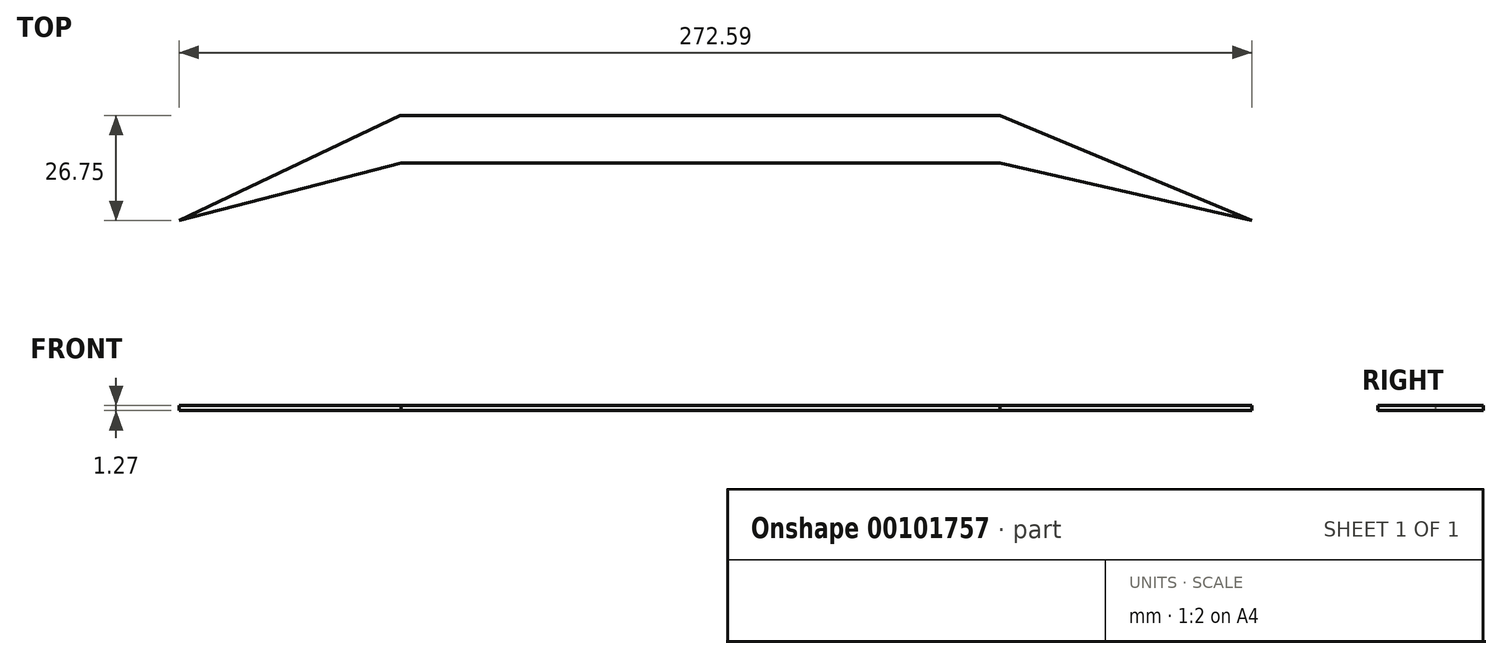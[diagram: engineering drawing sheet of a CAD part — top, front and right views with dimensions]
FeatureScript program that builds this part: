
annotation { "Feature Type Name" : "Feature", "Feature Type Description" : "" }
export const myFeature = defineFeature(function(context is Context, id is Id, definition is map)
    precondition{}
    {
        {
            var Q0;
            Q0=qCreatedBy(makeId("Top.planeOp"),FACE);
            var sketch = newSketch(context, id + "F0", { "sketchPlane" : qUnion([Q0])});
            skLineSegment(sketch, "E0", {"start": v(-136.18, 0) * mm, "end": v(-80.07, 26.75) * mm});
            skLineSegment(sketch, "E1", {"start": v(-80.07, 26.75) * mm, "end": v(0, 26.75) * mm});
            skLineSegment(sketch, "E2", {"start": v(0, 26.75) * mm, "end": v(72.33, 26.75) * mm});
            skLineSegment(sketch, "E3", {"start": v(72.33, 26.75) * mm, "end": v(136.4, 0) * mm});
            skLineSegment(sketch, "E4", {"start": v(136.4, 0) * mm, "end": v(72.33, 14.63) * mm});
            skLineSegment(sketch, "E5", {"start": v(72.33, 14.63) * mm, "end": v(0, 14.63) * mm});
            skLineSegment(sketch, "E6", {"start": v(0, 14.63) * mm, "end": v(-79.72, 14.63) * mm});
            skLineSegment(sketch, "E7", {"start": v(-79.72, 14.63) * mm, "end": v(-136.18, 0) * mm});
            skSolve(sketch);
        }
        {
            var Q0;
            Q0=makeQuery(id+"F0.imprint","IMPRINT",FACE,{"disambiguationData":[TD([[makeQuery(id+"F0.imprint","IMPRINT",EDGE,{"derivedFrom":sQuery(id+"F0.wireOp",EDGE,"E0")}),-1.0]])]});
            extrude(context, id + "F1", {"entities" : qUnion([Q0]), "depth" : 1.27 * mm});
        }
    });
